# Revit family: Sanitary_Accessories_DURAVIT-AG_D-Code-Toilet-paper-holder-165x66x99-mm2
name_source: partatom
category: Generic Models
revit_build: Autodesk Revit 2018 (Build: 20190510_1515(x64)
units: mm (PartAtom-declared; Revit-internal decimal feet)

## family parameters
Can host rebar = No
Cut with Voids When Loaded = No
Host = Face
OmniClass Number = 23.31.19.00
OmniClass Title = Toilets
Part Type = Normal
Room Calculation Point = No
Round Connector Dimension = Use Diameter
Shared = No

## types (1)
- D-Code Toilet paper holder 165x66x99 mm - 009926
    BIMobject category = Bathroom Accessories
    Default Elevation = 1219 mm
    Description = Duravit D-Code Toilet paper holder Chrome 165x165x99 mm - 0099261000
    Design country = Germany
    ETIM classification = EC010553 | Toilet roll holder
    Edition number = 1
    IFC Classification = Furnishing Element
    Installation instructions = https://pro.duravit.com
    Main material = Duravit - Metal - 10 - Chrome
    Manufacturer = Duravit
    Manufacturer country = Germany
    Manufacturer name = DURAVIT AG
    Masterformat 2014 Code = 01 52 19
    Masterformat 2014 Description = Sanitary Facilities
    Material main = Brass
    Model = D-Code Toilet paper holder 165x66x99 mm - 009926
    OmniClass Code = 23-31 19 00
    OmniClass Description = Toilets
    Product Guid = bb25b041-dd13-410e-9c4e-5453349ba85f
    Product SKU = D-Code-Toilet-paper-holder-165x165x99-mm-009926
    Product certification = https://pro.duravit.com
    Product data url = https://bimobject.com
    Product family = Bathtubs & Wellbeing
    Product group = Toilet paper holder
    Product name = D-Code Toilet paper holder 165x66x99 mm - 009926
    Product url = https://pro.duravit.com
    QR code = https://bimobject.com
    Technical description = https://pro.duravit.com
    UNSPSC Code = 301815
    URL = https://www.duravit.com
    Uniclass 2015 Code = Pr_40_20_93
    Uniclass 2015 Name = Urinal and WC fittings
    Uniformat II Code = D2030
    Uniformat II Description = Sanitary Waste
    Weight Net (Kg) = 0.4
    Youtube clip = https://pro.duravit.com

## geometry (parser evidence)
native form markers: Sweep x3
no freeform markers — native parametric forms only
